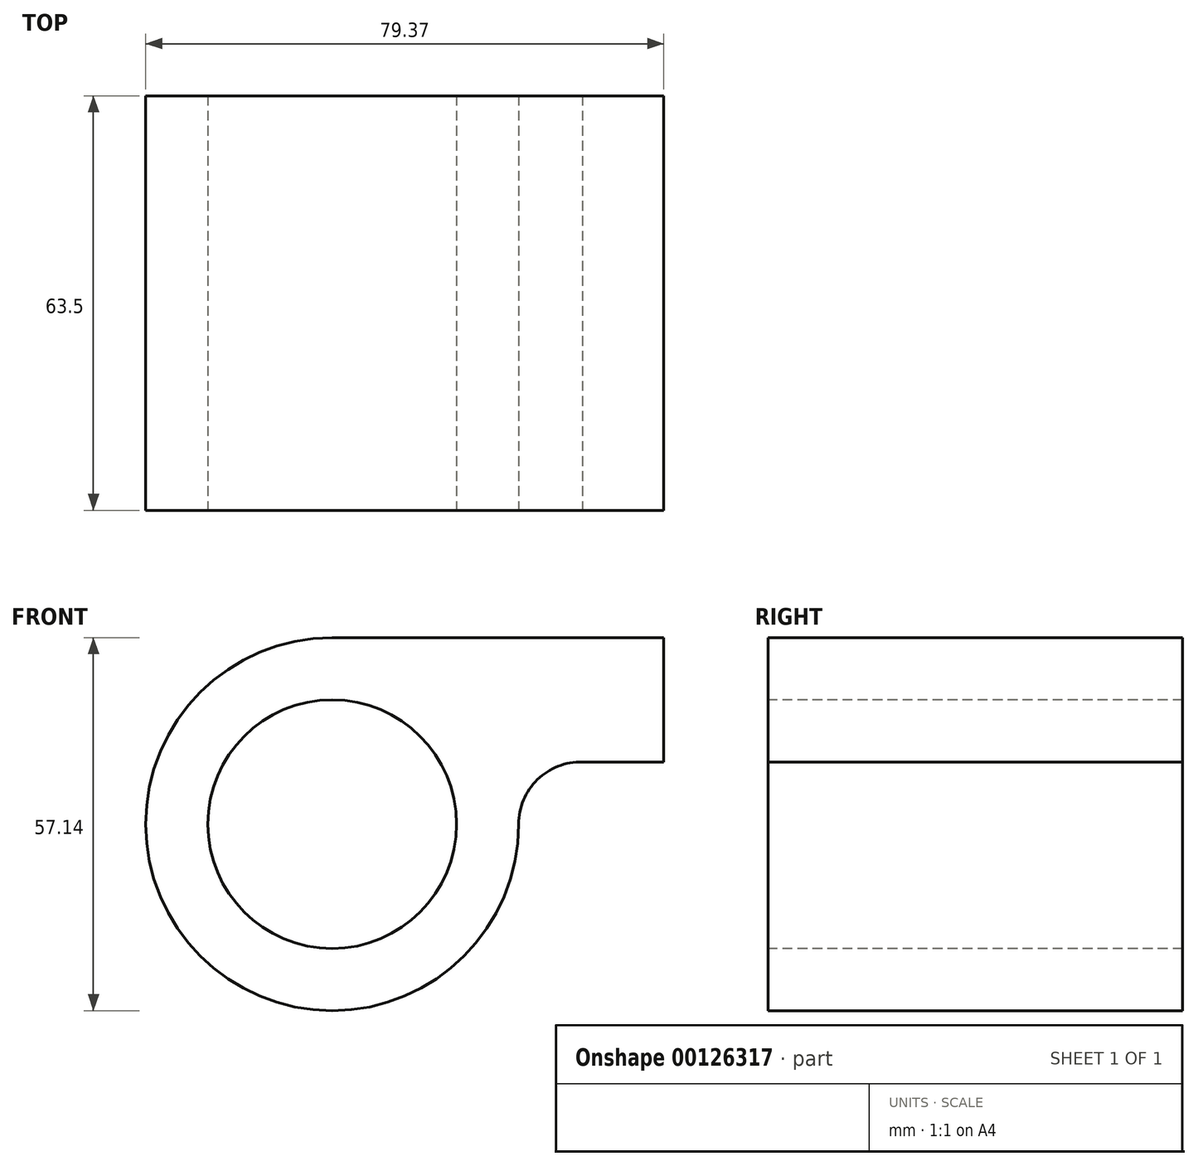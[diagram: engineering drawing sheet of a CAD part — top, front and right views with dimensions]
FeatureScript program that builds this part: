
annotation { "Feature Type Name" : "Feature", "Feature Type Description" : "" }
export const myFeature = defineFeature(function(context is Context, id is Id, definition is map)
    precondition{}
    {
        {
            var Q0;
            Q0=qCreatedBy(makeId("Front.planeOp"),FACE);
            var sketch = newSketch(context, id + "F0", { "sketchPlane" : qUnion([Q0])});
            skArc(sketch, "E0", {"start": v(28.58, 0) * mm, "mid": v(-20.2, -20.2) * mm, "end": v(0, 28.58) * mm});
            skCircle(sketch, "E1", {"center": v(0, 0) * mm, "radius": 19.05 * mm});
            skArc(sketch, "E2", {"start": v(28.58, 0) * mm, "mid": v(31.45, 6.82) * mm, "end": v(38.33, 9.52) * mm});
            skLineSegment(sketch, "E3", {"start": v(0, 28.58) * mm, "end": v(50.8, 28.58) * mm});
            skLineSegment(sketch, "E4", {"start": v(50.8, 28.58) * mm, "end": v(50.8, 9.52) * mm});
            skLineSegment(sketch, "E5", {"start": v(50.8, 9.52) * mm, "end": v(38.33, 9.52) * mm});
            skLineSegment(sketch, "E6", {"start": v(69.85, 9.52) * mm, "end": v(15, -24.32) * mm});
            skLineSegment(sketch, "E7", {"start": v(69.85, 9.52) * mm, "end": v(50.8, 9.52) * mm});
            skSolve(sketch);
        }
        {
            var Q0;
            Q0=makeQuery(id+"F0.imprint","IMPRINT",FACE,{"disambiguationData":[TD([[makeQuery(id+"F0.imprint","IMPRINT",EDGE,{"derivedFrom":sQuery(id+"F0.wireOp",EDGE,"E1")}),-1.0]])]});
            extrude(context, id + "F1", {"entities" : qUnion([Q0]), "endBound" : BoundingType.SYMMETRIC, "oppositeDirection" : true, "depth" : 63.5 * mm});
        }
        {
            var Q0;
            {var subQ1=sQuery(id+"F0.wireOp",EDGE,"E2");Q0=makeQuery(id+"F0.imprint","IMPRINT",FACE,{"disambiguationData":[TD([[makeQuery(id+"F0.imprint","IMPRINT",EDGE,{"derivedFrom":subQ1}),-1.0]])]});}
            extrude(context, id + "F2", {"entities" : qUnion([Q0]), "operationType" : NewBodyOperationType.ADD, "endBound" : BoundingType.SYMMETRIC, "oppositeDirection" : true, "depth" : 9.52 * mm});
        }
    });
